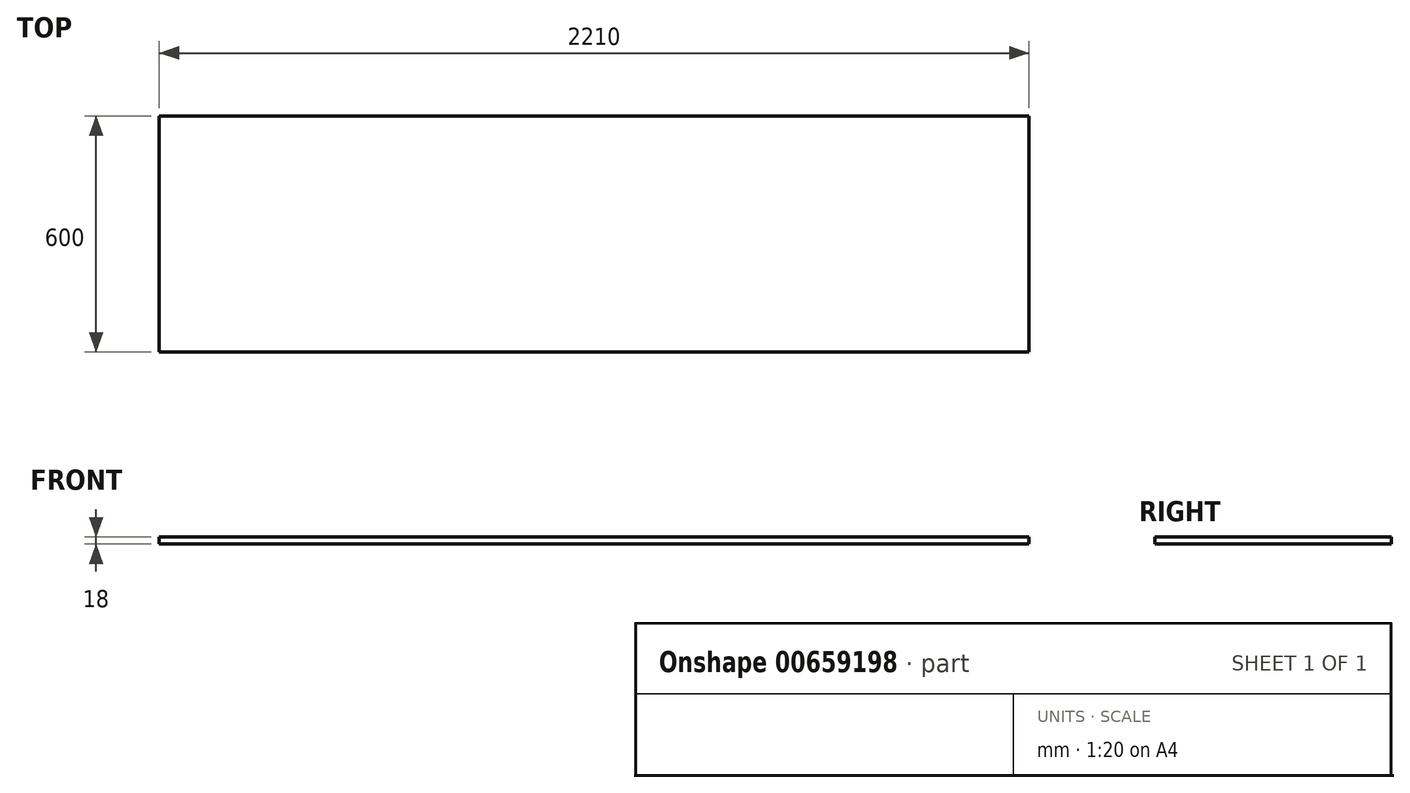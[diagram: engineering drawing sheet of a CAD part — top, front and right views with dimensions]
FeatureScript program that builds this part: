
annotation { "Feature Type Name" : "Feature", "Feature Type Description" : "" }
export const myFeature = defineFeature(function(context is Context, id is Id, definition is map)
    precondition{}
    {
        {
            var Q0;
            Q0=qCreatedBy(makeId("Top.planeOp"),FACE);
            var sketch = newSketch(context, id + "F0", { "sketchPlane" : qUnion([Q0])});
            skLineSegment(sketch, "E0.bottom", {"start": v(-261.85, 301.9) * mm, "end": v(1948.15, 301.9) * mm});
            skLineSegment(sketch, "E0.top", {"start": v(-261.85, -298.1) * mm, "end": v(1948.15, -298.1) * mm});
            skLineSegment(sketch, "E0.left", {"start": v(-261.85, 301.9) * mm, "end": v(-261.85, -298.1) * mm});
            skLineSegment(sketch, "E0.right", {"start": v(1948.15, 301.9) * mm, "end": v(1948.15, -298.1) * mm});
            skSolve(sketch);
        }
        {
            var Q0;
            Q0 = qSketchRegion(id + "F0", true);
            extrude(context, id + "F1", {"entities" : qUnion([Q0]), "endBound" : BoundingType.SYMMETRIC, "depth" : 18 * mm, "offsetDistance" : 25 * mm});
        }
    });
